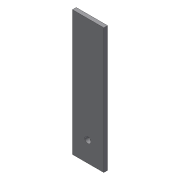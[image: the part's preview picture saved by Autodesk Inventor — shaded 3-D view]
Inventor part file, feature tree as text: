
AUTODESK INVENTOR PART (.ipt)
format: ipt  version: 2019.4 (Build 234330000, 330)  size: 135,168 bytes
history: native  units: mm
features: reference x5, other x4, hole x3, sketch x2, extrude x1, fillet x1
ambient origin geometry x8: Origin, YZ Plane, XZ Plane, XY Plane, X Axis, Y Axis, Z Axis, Center Point
bodies: Body1 (feature_tree)
feature tree (16):
  other  "ソリッド1"
  sketch  "スケッチ1"
  extrude  "押し出し1"  Depth=2.0mm TaperAngle=0.0deg
  hole  "穴2"  [1 undecoded]
  hole  "穴3"  [1 undecoded]
  fillet  "フィレット1"  Radius=3.5mm
  hole  "穴4"  [1 undecoded]
  reference  "参照1"
  reference  "参照2"
  reference  "参照3"
  reference  "参照4"
  reference  "参照5"
  sketch  "スケッチ2"
  other  "Assembly1"
  other  "XM540_NO_BACK:1"
  other  "XM540_HOUSING_TOP:1"
note: 3 required parameter values undecoded (feature->parameter linkage not recoverable at this tier; creation-order binding heuristic only, values carry confidence <= 0.55)
